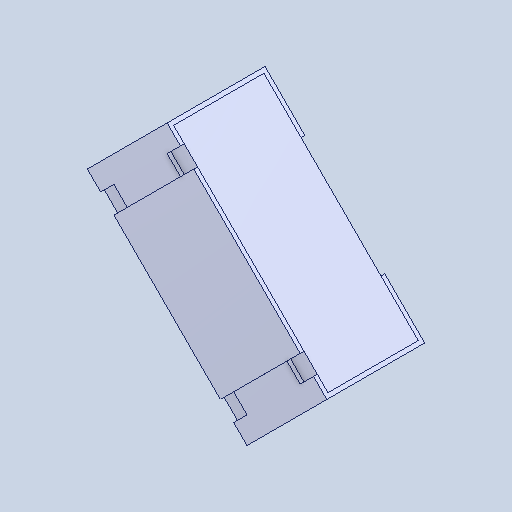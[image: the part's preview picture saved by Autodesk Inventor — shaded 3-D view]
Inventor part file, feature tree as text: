
AUTODESK INVENTOR PART (.ipt)
format: ipt  version: 2025 (Build 290162000, 162)  size: 107,520 bytes
history: native  units: mm
features: boolean_combine x2, other x1, mirror x1
ambient origin geometry x8: Origin, YZ Plane, XZ Plane, XY Plane, X Axis, Y Axis, Z Axis, Center Point
bodies: Solid1 (feature_tree), Solid2 (feature_tree), Solid3 (feature_tree), Solid4 (feature_tree)
feature tree (4):
  other  "Cut-Extrude1"
  boolean_combine  "Combine2"
  mirror  "Mirror1[3]"
  boolean_combine  "Combine1"
